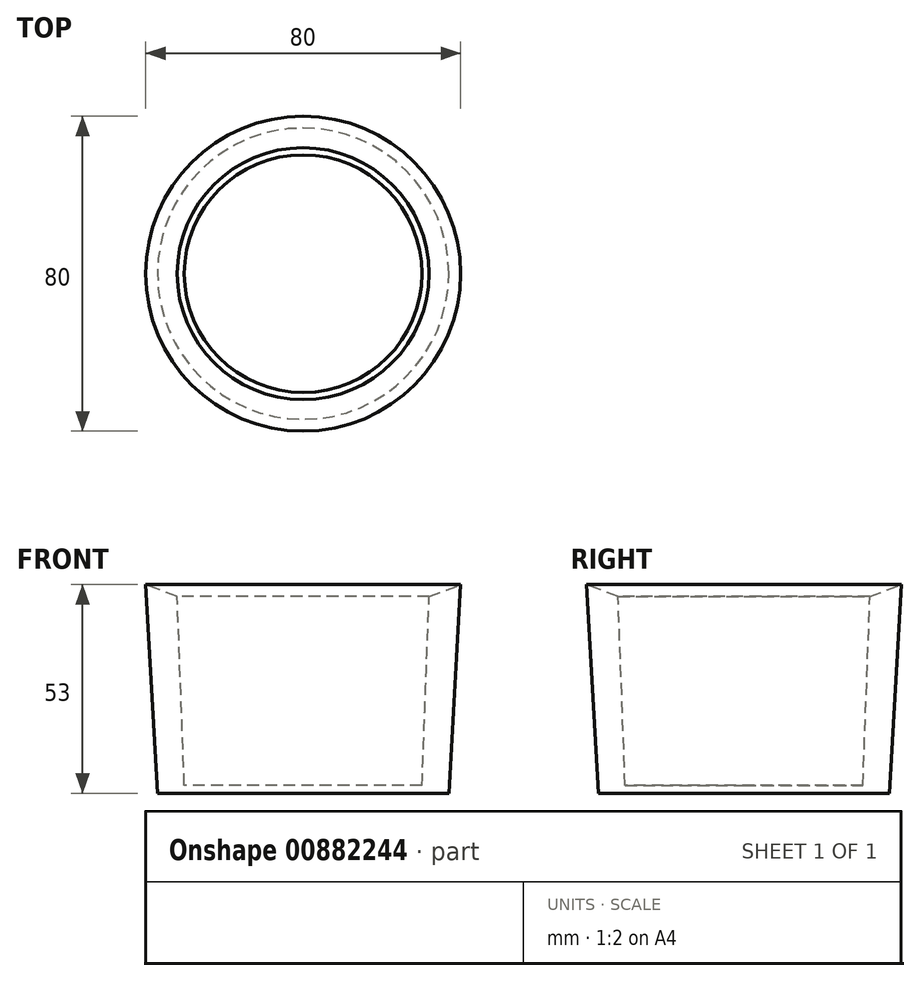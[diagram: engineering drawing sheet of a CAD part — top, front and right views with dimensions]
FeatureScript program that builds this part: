
annotation { "Feature Type Name" : "Feature", "Feature Type Description" : "" }
export const myFeature = defineFeature(function(context is Context, id is Id, definition is map)
    precondition{}
    {
        {
            var Q0;
            Q0=qCreatedBy(makeId("Right.planeOp"),FACE);
            var sketch = newSketch(context, id + "F0", { "sketchPlane" : qUnion([Q0])});
            skLineSegment(sketch, "E0", {"start": v(-40, 53) * mm, "end": v(-32, 49.96) * mm});
            skLineSegment(sketch, "E1", {"start": v(-30, 0) * mm, "end": v(-37, 0) * mm});
            skLineSegment(sketch, "E2", {"start": v(-37, 0) * mm, "end": v(-40, 53) * mm});
            skLineSegment(sketch, "E3", {"start": v(-30.2, 2) * mm, "end": v(0, 2) * mm});
            skLineSegment(sketch, "E4", {"start": v(0, 2) * mm, "end": v(0, 0) * mm});
            skLineSegment(sketch, "E5", {"start": v(0, 0) * mm, "end": v(-30, 0) * mm});
            skLineSegment(sketch, "E6", {"start": v(-32, 49.96) * mm, "end": v(-30.2, 2) * mm});
            skSolve(sketch);
        }
        {
            var Q0;
            Q0=makeQuery(id+"F0.imprint","IMPRINT",FACE,{"disambiguationData":[TD([[makeQuery(id+"F0.imprint","IMPRINT",EDGE,{"derivedFrom":sQuery(id+"F0.wireOp",EDGE,"E0")}),-1.0]])]});
            var Q1;
            Q1=sQuery(id+"F0.wireOp",EDGE,"E4");
            revolve(context, id + "F1", {"surfaceOperationType" : NewSurfaceOperationType.NEW, "entities" : qUnion([Q0]), "axis" : qUnion([Q1]), "revolveType" : RevolveType.FULL});
        }
    });
